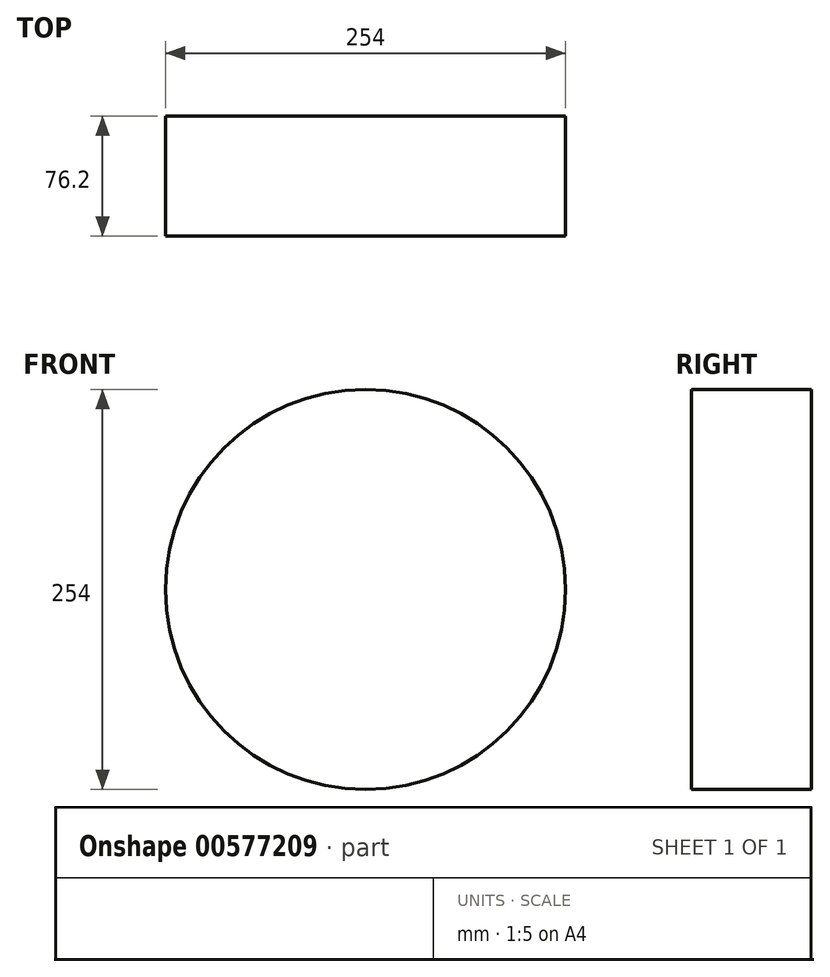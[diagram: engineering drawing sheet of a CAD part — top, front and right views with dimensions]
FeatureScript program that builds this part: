
annotation { "Feature Type Name" : "Feature", "Feature Type Description" : "" }
export const myFeature = defineFeature(function(context is Context, id is Id, definition is map)
    precondition{}
    {
        {
            var Q0;
            Q0=qCreatedBy(makeId("Front.planeOp"),FACE);
            var sketch = newSketch(context, id + "F0", { "sketchPlane" : qUnion([Q0])});
            skCircle(sketch, "E0", {"center": v(0, 0) * mm, "radius": 127 * mm});
            skSolve(sketch);
        }
        {
            var Q0;
            Q0 = qSketchRegion(id + "F0", true);
            extrude(context, id + "F1", {"entities" : qUnion([Q0]), "depth" : 76.2 * mm, "offsetDistance" : 25.4 * mm});
        }
    });
